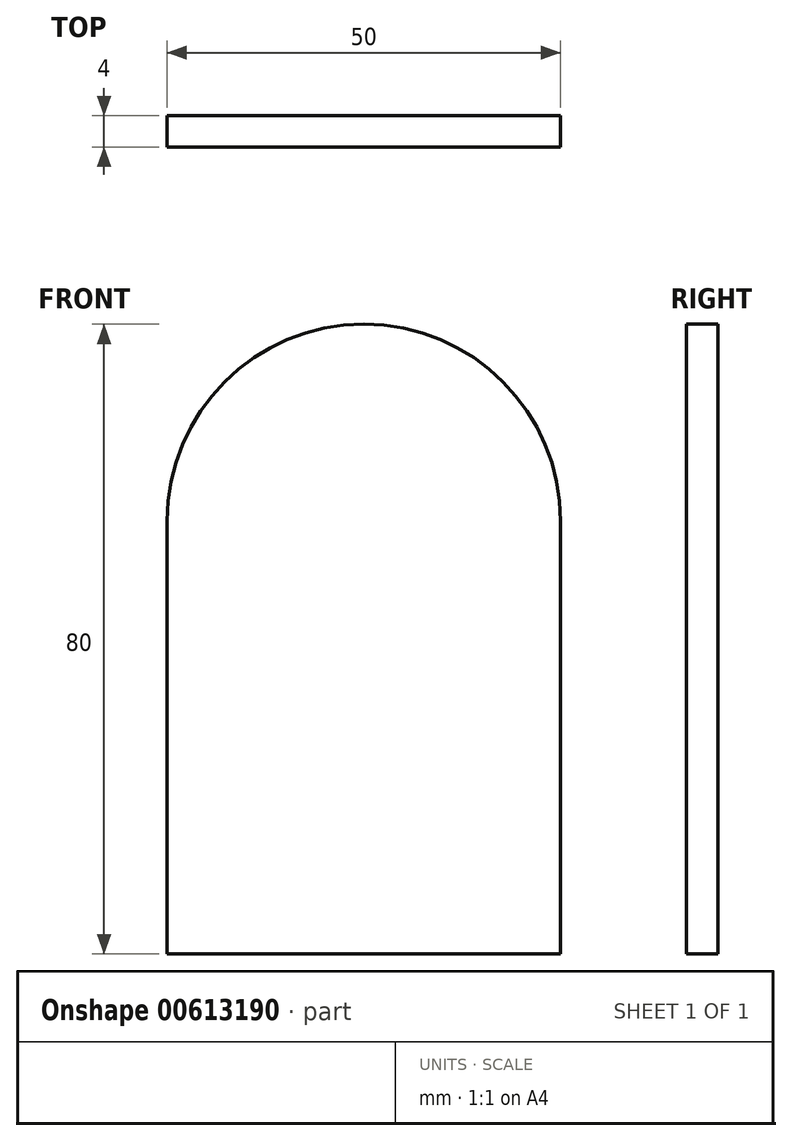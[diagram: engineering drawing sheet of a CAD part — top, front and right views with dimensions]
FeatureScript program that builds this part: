
annotation { "Feature Type Name" : "Feature", "Feature Type Description" : "" }
export const myFeature = defineFeature(function(context is Context, id is Id, definition is map)
    precondition{}
    {
        {
            var Q0;
            Q0=qCreatedBy(makeId("Front.planeOp"),FACE);
            var sketch = newSketch(context, id + "F0", { "sketchPlane" : qUnion([Q0])});
            skLineSegment(sketch, "E0.bottom", {"start": v(0, 0) * mm, "end": v(50, 0) * mm});
            skLineSegment(sketch, "E0.left", {"start": v(0, 0) * mm, "end": v(0, 55) * mm});
            skLineSegment(sketch, "E0.right", {"start": v(50, 0) * mm, "end": v(50, 55) * mm});
            skArc(sketch, "E1", {"start": v(50, 55) * mm, "mid": v(25, 80) * mm, "end": v(0, 55) * mm});
            skSolve(sketch);
        }
        {
            var Q0;
            Q0=makeQuery(id+"F0.imprint","IMPRINT",FACE,{"disambiguationData":[TD([[makeQuery(id+"F0.imprint","IMPRINT",EDGE,{"derivedFrom":sQuery(id+"F0.wireOp",EDGE,"E0.bottom")}),1.0]])]});
            extrude(context, id + "F1", {"entities" : qUnion([Q0]), "depth" : 4 * mm, "offsetDistance" : 25 * mm});
        }
    });
